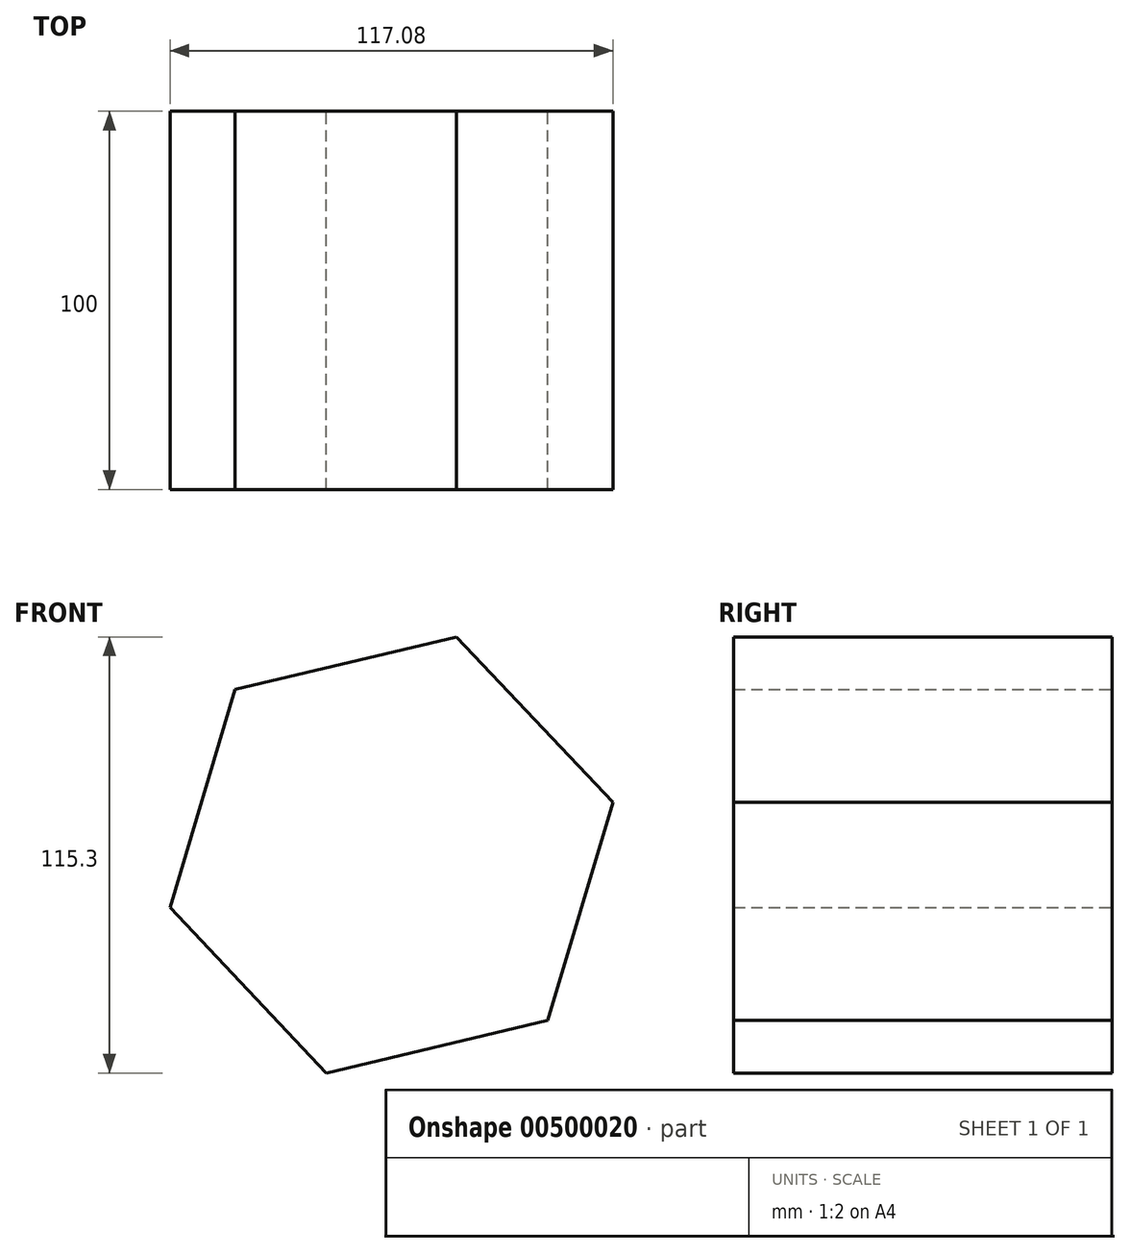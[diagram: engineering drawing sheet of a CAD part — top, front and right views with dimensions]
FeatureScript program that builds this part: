
annotation { "Feature Type Name" : "Feature", "Feature Type Description" : "" }
export const myFeature = defineFeature(function(context is Context, id is Id, definition is map)
    precondition{}
    {
        {
            var Q0;
            Q0=qCreatedBy(makeId("Front.planeOp"),FACE);
            var sketch = newSketch(context, id + "F0", { "sketchPlane" : qUnion([Q0])});
            skCircle(sketch, "E0.cCircle", {"center": v(0, 0) * mm, "radius": 60.17 * mm, "construction": true});
            skLineSegment(sketch, "E0.0", {"start": v(-41.31, 43.75) * mm, "end": v(17.23, 57.65) * mm});
            skLineSegment(sketch, "E0.1", {"start": v(17.23, 57.65) * mm, "end": v(58.54, 13.9) * mm});
            skLineSegment(sketch, "E0.2", {"start": v(58.54, 13.9) * mm, "end": v(41.31, -43.75) * mm});
            skLineSegment(sketch, "E0.3", {"start": v(41.31, -43.75) * mm, "end": v(-17.23, -57.65) * mm});
            skLineSegment(sketch, "E0.4", {"start": v(-17.23, -57.65) * mm, "end": v(-58.54, -13.9) * mm});
            skLineSegment(sketch, "E0.5", {"start": v(-58.54, -13.9) * mm, "end": v(-41.31, 43.75) * mm});
            skSolve(sketch);
        }
        {
            var Q0;
            Q0=makeQuery(id+"F0.imprint","IMPRINT",FACE,{"disambiguationData":[TD([[makeQuery(id+"F0.imprint","IMPRINT",EDGE,{"derivedFrom":sQuery(id+"F0.wireOp",EDGE,"E0.0")}),-1.0]])]});
            extrude(context, id + "F1", {"entities" : qUnion([Q0]), "endBound" : BoundingType.SYMMETRIC, "depth" : 100 * mm});
        }
    });
